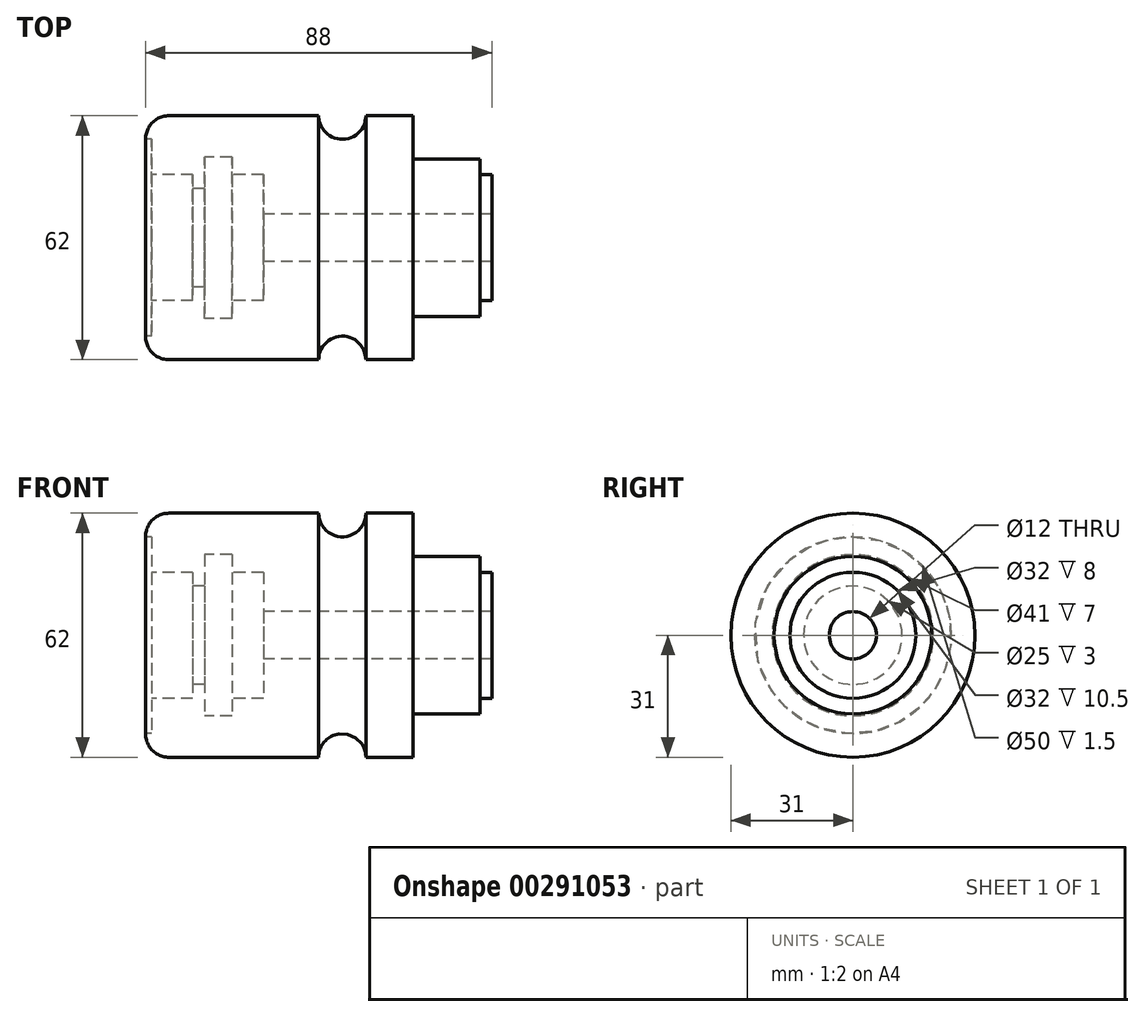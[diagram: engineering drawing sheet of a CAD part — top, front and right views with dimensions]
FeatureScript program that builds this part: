
annotation { "Feature Type Name" : "Feature", "Feature Type Description" : "" }
export const myFeature = defineFeature(function(context is Context, id is Id, definition is map)
    precondition{}
    {
        {
            var Q0;
            Q0=qCreatedBy(makeId("Front.planeOp"),FACE);
            var sketch = newSketch(context, id + "F0", { "sketchPlane" : qUnion([Q0])});
            skLineSegment(sketch, "E0", {"start": v(0, 0) * mm, "end": v(0, 31) * mm});
            skLineSegment(sketch, "E1", {"start": v(0, 31) * mm, "end": v(44, 31) * mm});
            skLineSegment(sketch, "E2", {"start": v(68, 31) * mm, "end": v(68, 20) * mm});
            skLineSegment(sketch, "E3", {"start": v(68, 20) * mm, "end": v(85, 20) * mm});
            skLineSegment(sketch, "E4", {"start": v(85, 20) * mm, "end": v(85, 16) * mm});
            skLineSegment(sketch, "E5", {"start": v(85, 16) * mm, "end": v(88, 16) * mm});
            skLineSegment(sketch, "E6", {"start": v(88, 16) * mm, "end": v(88, 0) * mm});
            skLineSegment(sketch, "E7", {"start": v(0, 0) * mm, "end": v(110.42, 0) * mm, "construction": true});
            skArc(sketch, "E8", {"start": v(44, 31) * mm, "mid": v(50, 25) * mm, "end": v(56, 31) * mm});
            skLineSegment(sketch, "E9.trimOffspring", {"start": v(56, 31) * mm, "end": v(68, 31) * mm});
            skLineSegment(sketch, "E10", {"start": v(0, 0) * mm, "end": v(88, 0) * mm});
            skSolve(sketch);
        }
        {
            var Q0;
            Q0 = qSketchRegion(id + "F0", true);
            var Q1;
            Q1=sQuery(id+"F0.wireOp",EDGE,"E7");
            revolve(context, id + "F1", {"entities" : qUnion([Q0]), "axis" : qUnion([Q1]), "revolveType" : RevolveType.FULL});
        }
        {
            var Q0;
            Q0=qCreatedBy(makeId("Front.planeOp"),FACE);
            var sketch = newSketch(context, id + "F2", { "sketchPlane" : qUnion([Q0])});
            skLineSegment(sketch, "E11", {"start": v(0, 0) * mm, "end": v(0, 25) * mm});
            skLineSegment(sketch, "E12", {"start": v(0, 25) * mm, "end": v(1.5, 25) * mm});
            skLineSegment(sketch, "E13", {"start": v(1.5, 25) * mm, "end": v(1.5, 16) * mm});
            skLineSegment(sketch, "E14", {"start": v(1.5, 16) * mm, "end": v(12, 16) * mm});
            skLineSegment(sketch, "E15", {"start": v(12, 16) * mm, "end": v(12, 12.5) * mm});
            skLineSegment(sketch, "E16", {"start": v(12, 12.5) * mm, "end": v(15, 12.5) * mm});
            skLineSegment(sketch, "E17", {"start": v(15, 12.5) * mm, "end": v(15, 20.5) * mm});
            skLineSegment(sketch, "E18", {"start": v(15, 20.5) * mm, "end": v(22, 20.5) * mm});
            skLineSegment(sketch, "E19", {"start": v(22, 20.5) * mm, "end": v(22, 16) * mm});
            skLineSegment(sketch, "E20", {"start": v(22, 16) * mm, "end": v(30, 16) * mm});
            skLineSegment(sketch, "E21", {"start": v(30, 16) * mm, "end": v(30, 6) * mm});
            skLineSegment(sketch, "E22", {"start": v(30, 6) * mm, "end": v(88, 6) * mm});
            skLineSegment(sketch, "E23", {"start": v(88, 6) * mm, "end": v(88, 0) * mm});
            skLineSegment(sketch, "E24", {"start": v(88, 0) * mm, "end": v(0, 0) * mm});
            skLineSegment(sketch, "E25", {"start": v(0, 0) * mm, "end": v(-28.25, 0) * mm, "construction": true});
            skSolve(sketch);
        }
        {
            var Q0;
            Q0 = qSketchRegion(id + "F2", true);
            var Q1;
            Q1=sQuery(id+"F2.wireOp",EDGE,"E25");
            revolve(context, id + "F3", {"operationType" : NewBodyOperationType.REMOVE, "entities" : qUnion([Q0]), "axis" : qUnion([Q1]), "revolveType" : RevolveType.FULL, "oppositeDirection" : true});
        }
        {
            var Q0;
            Q0=makeQuery(id+"F1.opRevolve","SWEPT_EDGE",EDGE,{"disambiguationData":[OSD([sQuery(id+"F0.wireOp",EDGE,"E0"),sQuery(id+"F0.wireOp",EDGE,"E1")])]});
            fillet(context, id + "F4", {"entities" : qUnion([Q0]), "radius" : 6 * mm, "tangentPropagation" : true, "allowEdgeOverflow" : false});
        }
    });
